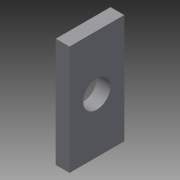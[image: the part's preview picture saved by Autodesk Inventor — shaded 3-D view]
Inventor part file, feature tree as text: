
AUTODESK INVENTOR PART (.ipt)
format: ipt  version: 2013 (Build 170138000, 138)  size: 86,016 bytes
history: native  units: in
note: dims shown in document units (in); Inventor stores cm internally (conversion verified against a paired STEP export)
features: extrude x2, sketch x2
ambient origin geometry x8: Origin, YZ Plane, XZ Plane, XY Plane, X Axis, Y Axis, Z Axis, Center Point
feature tree (4):
  extrude  "Extrusion2"  Depth=1.0in
  extrude  "Extrusion3"  Depth=2.5in
  sketch  "Sketch1"  dims[d0=4.5in d1=1.0in]
  sketch  "Sketch2"  dims[d4=1.0in d5=2.5in d6=0.25in d7=0.5in d8=0.25in d9=0.0in d10=2.5in d11=1.0in d12=0.0in]
